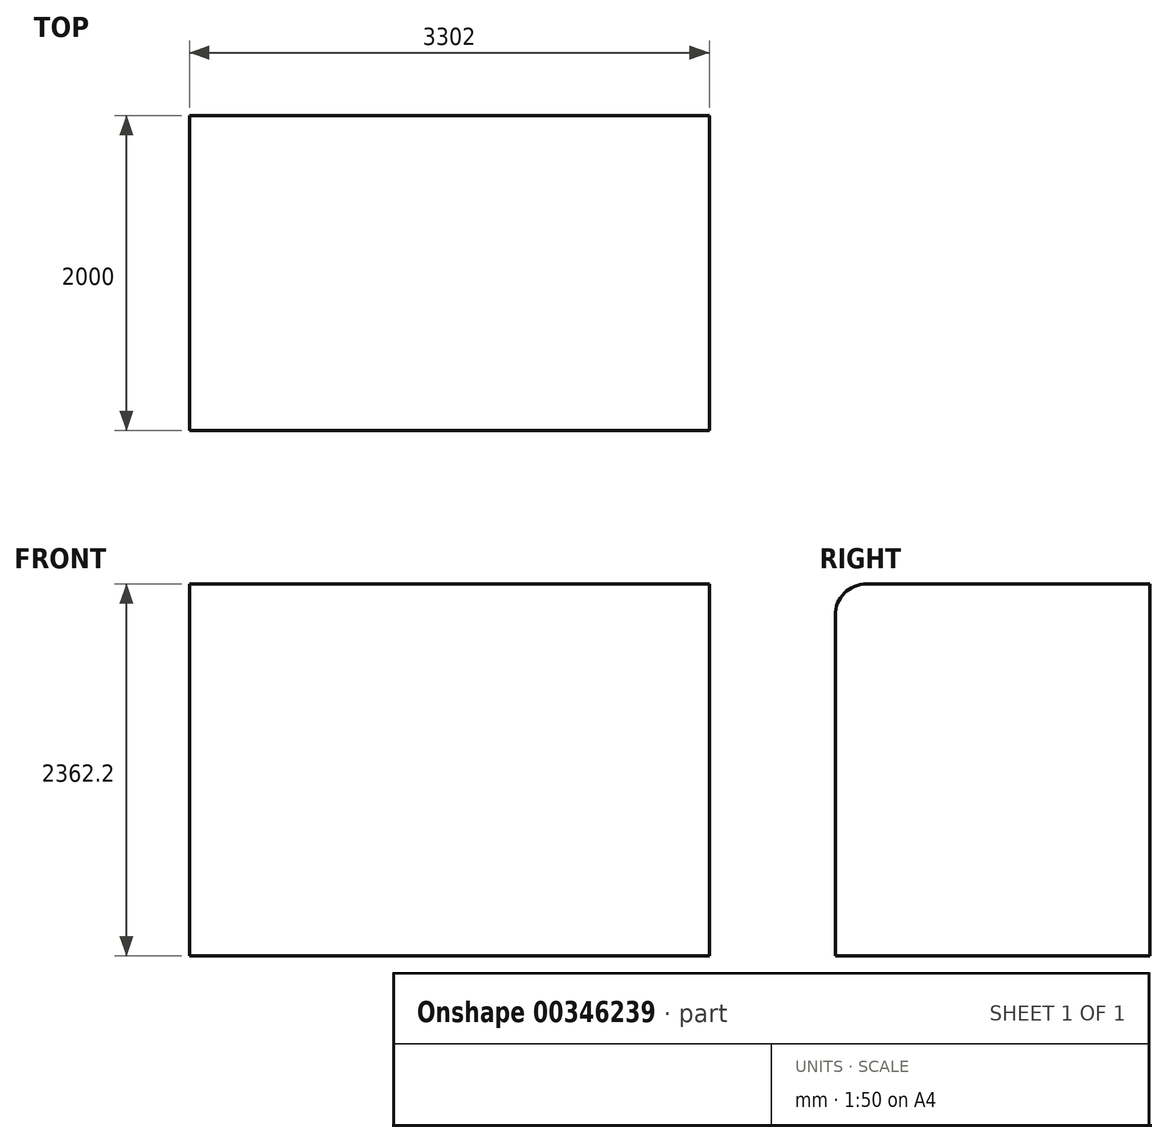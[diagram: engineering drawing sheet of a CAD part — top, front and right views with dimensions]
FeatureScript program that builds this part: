
annotation { "Feature Type Name" : "Feature", "Feature Type Description" : "" }
export const myFeature = defineFeature(function(context is Context, id is Id, definition is map)
    precondition{}
    {
        {
            var Q0;
            Q0=qCreatedBy(makeId("Front.planeOp"),FACE);
            var sketch = newSketch(context, id + "F0", { "sketchPlane" : qUnion([Q0])});
            skLineSegment(sketch, "E0.bottom", {"start": v(2044.95, 2309.6) * mm, "end": v(-1257.05, 2309.6) * mm});
            skLineSegment(sketch, "E0.top", {"start": v(2044.95, -52.6) * mm, "end": v(-1257.05, -52.6) * mm});
            skLineSegment(sketch, "E0.left", {"start": v(2044.95, 2309.6) * mm, "end": v(2044.95, -52.6) * mm});
            skLineSegment(sketch, "E0.right", {"start": v(-1257.05, 2309.6) * mm, "end": v(-1257.05, -52.6) * mm});
            skSolve(sketch);
        }
        {
            var Q0;
            Q0=makeQuery(id+"F0.imprint","IMPRINT",FACE,{"disambiguationData":[TD([[makeQuery(id+"F0.imprint","IMPRINT",EDGE,{"derivedFrom":sQuery(id+"F0.wireOp",EDGE,"E0.bottom")}),1.0]])]});
            extrude(context, id + "F1", {"entities" : qUnion([Q0]), "depth" : 25.4 * mm});
        }
        {
            var Q0;
            Q0=makeQuery(id+"F1.opExtrude","CAP_FACE",FACE,{"disambiguationData":[OSD([sQuery(id+"F0.wireOp",EDGE,"E0.bottom"),sQuery(id+"F0.wireOp",EDGE,"E0.top"),sQuery(id+"F0.wireOp",EDGE,"E0.left"),sQuery(id+"F0.wireOp",EDGE,"E0.right")])],"isStart":false});
            extrude(context, id + "F2", {"entities" : qUnion([Q0]), "operationType" : NewBodyOperationType.ADD, "endBound" : BoundingType.SYMMETRIC, "depth" : 2000 * mm});
        }
        {
            var Q0;
            Q0=makeQuery(id+"F2.opExtrude","CAP_EDGE",EDGE,{"disambiguationData":[OSD([sQuery(id+"F0.wireOp",EDGE,"E0.bottom")])],"isStart":false});
            fillet(context, id + "F3", {"entities" : qUnion([Q0]), "radius" : 200 * mm, "allowEdgeOverflow" : false});
        }
    });
